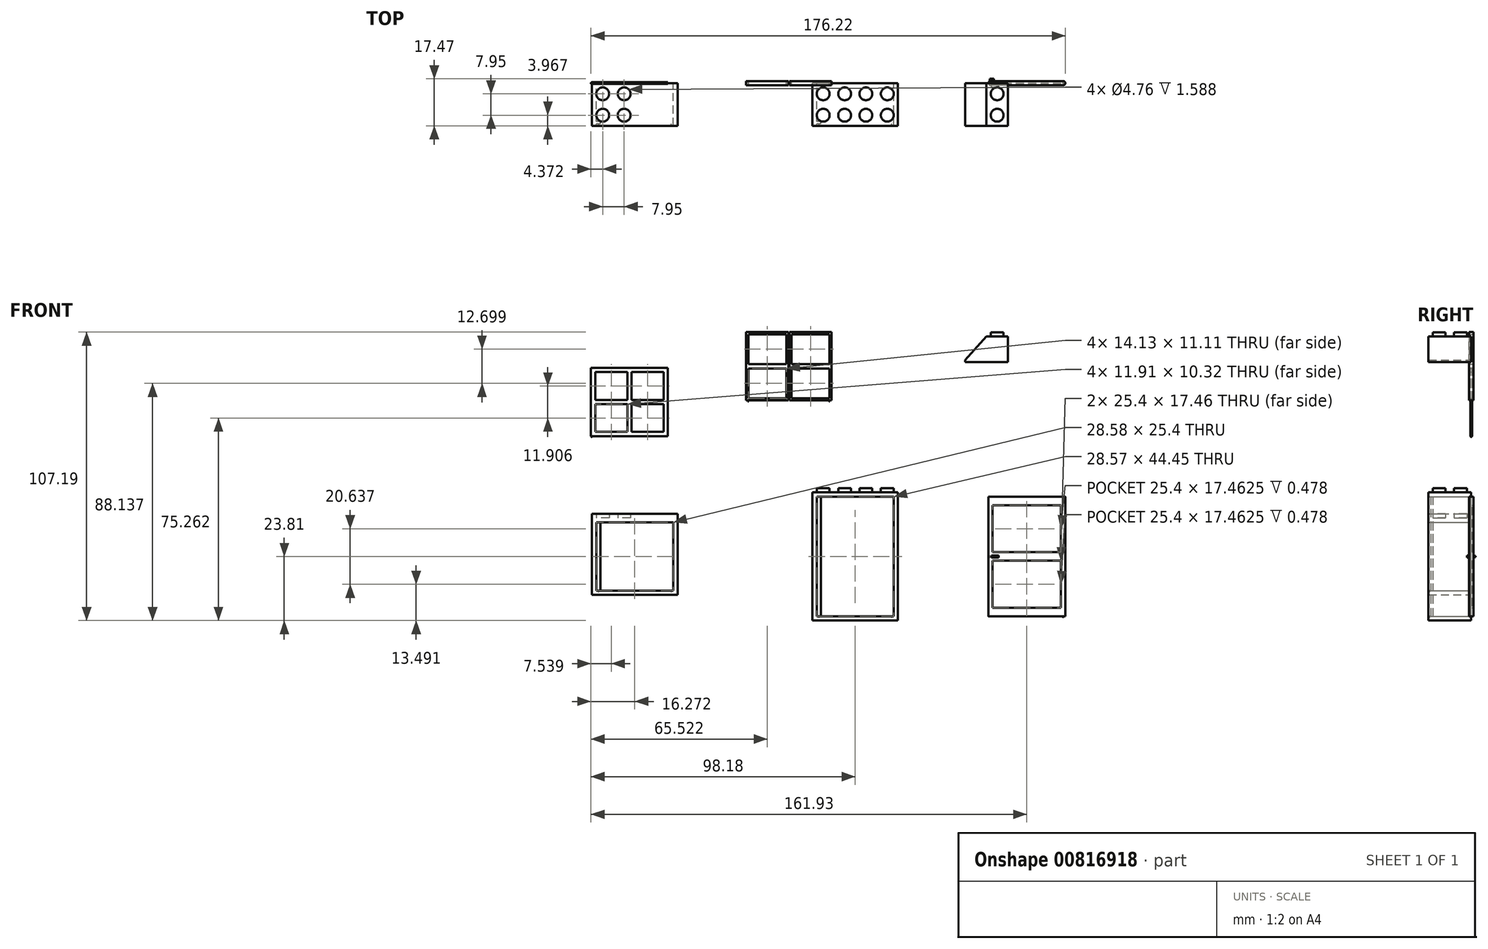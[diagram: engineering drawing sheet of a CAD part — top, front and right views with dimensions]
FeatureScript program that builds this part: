
annotation { "Feature Type Name" : "Feature", "Feature Type Description" : "" }
export const myFeature = defineFeature(function(context is Context, id is Id, definition is map)
    precondition{}
    {
        {
            var Q0;
            Q0=qCreatedBy(makeId("Front.planeOp"),FACE);
            var sketch = newSketch(context, id + "F0", { "sketchPlane" : qUnion([Q0])});
            skLineSegment(sketch, "E0.bottom", {"start": v(15.88, -23.81) * mm, "end": v(-15.87, -23.81) * mm});
            skLineSegment(sketch, "E0.top", {"start": v(15.87, 23.81) * mm, "end": v(-15.88, 23.81) * mm});
            skLineSegment(sketch, "E0.left", {"start": v(15.88, -23.81) * mm, "end": v(15.87, 23.81) * mm});
            skLineSegment(sketch, "E0.right", {"start": v(-15.87, -23.81) * mm, "end": v(-15.88, 23.81) * mm});
            skPoint(sketch, "E0.middle", {"position": v(0, 0) * mm});
            skLineSegment(sketch, "E1.bottom", {"start": v(14.29, -22.22) * mm, "end": v(-14.29, -22.23) * mm});
            skLineSegment(sketch, "E1.top", {"start": v(14.29, 22.23) * mm, "end": v(-14.29, 22.23) * mm});
            skLineSegment(sketch, "E1.left", {"start": v(14.29, -22.22) * mm, "end": v(14.29, 22.23) * mm});
            skLineSegment(sketch, "E1.right", {"start": v(-14.29, -22.23) * mm, "end": v(-14.29, 22.23) * mm});
            skLineSegment(sketch, "E2.bottom", {"start": v(78.04, -22.23) * mm, "end": v(49.46, -22.23) * mm});
            skLineSegment(sketch, "E2.top", {"start": v(78.04, 22.23) * mm, "end": v(49.46, 22.23) * mm});
            skLineSegment(sketch, "E2.left", {"start": v(78.04, -22.23) * mm, "end": v(78.04, 22.23) * mm});
            skLineSegment(sketch, "E2.right", {"start": v(49.46, -22.23) * mm, "end": v(49.46, 22.23) * mm});
            skPoint(sketch, "E2.middle", {"position": v(63.75, 0) * mm});
            skLineSegment(sketch, "E3.bottom", {"start": v(76.45, 1.59) * mm, "end": v(51.05, 1.59) * mm});
            skLineSegment(sketch, "E3.top", {"start": v(76.45, 19.05) * mm, "end": v(51.05, 19.05) * mm});
            skLineSegment(sketch, "E3.left", {"start": v(76.45, 1.59) * mm, "end": v(76.45, 19.05) * mm});
            skLineSegment(sketch, "E3.right", {"start": v(51.05, 1.59) * mm, "end": v(51.05, 19.05) * mm});
            skPoint(sketch, "E3.middle", {"position": v(63.75, 10.32) * mm});
            skPoint(sketch, "E3.middle.positionSnap0", {"position": v(63.75, 22.23) * mm});
            skPoint(sketch, "E3.centerSnap0", {"position": v(63.75, 22.23) * mm});
            skLineSegment(sketch, "E4.bottom", {"start": v(76.45, -1.59) * mm, "end": v(51.05, -1.59) * mm});
            skLineSegment(sketch, "E4.top", {"start": v(76.45, -19.05) * mm, "end": v(51.05, -19.05) * mm});
            skLineSegment(sketch, "E4.left", {"start": v(76.45, -1.59) * mm, "end": v(76.45, -19.05) * mm});
            skLineSegment(sketch, "E4.right", {"start": v(51.05, -1.59) * mm, "end": v(51.05, -19.05) * mm});
            skPoint(sketch, "E4.middle", {"position": v(63.75, -10.32) * mm});
            skPoint(sketch, "E4.middle.positionSnap0", {"position": v(63.75, -22.23) * mm});
            skPoint(sketch, "E4.centerSnap0", {"position": v(63.75, -22.23) * mm});
            skLineSegment(sketch, "E5.bottom", {"start": v(-67.62, -12.7) * mm, "end": v(-96.2, -12.7) * mm});
            skLineSegment(sketch, "E5.top", {"start": v(-67.62, 12.7) * mm, "end": v(-96.2, 12.7) * mm});
            skLineSegment(sketch, "E5.left", {"start": v(-67.62, -12.7) * mm, "end": v(-67.62, 12.7) * mm});
            skLineSegment(sketch, "E5.right", {"start": v(-96.2, -12.7) * mm, "end": v(-96.2, 12.7) * mm});
            skPoint(sketch, "E5.middle", {"position": v(-81.9, 0) * mm});
            skLineSegment(sketch, "E6.bottom", {"start": v(-66.03, -14.29) * mm, "end": v(-97.78, -14.29) * mm});
            skLineSegment(sketch, "E6.top", {"start": v(-66.03, 14.29) * mm, "end": v(-97.78, 14.29) * mm});
            skLineSegment(sketch, "E6.left", {"start": v(-66.03, -14.29) * mm, "end": v(-66.03, 14.29) * mm});
            skLineSegment(sketch, "E6.right", {"start": v(-97.78, -14.29) * mm, "end": v(-97.78, 14.29) * mm});
            skLineSegment(sketch, "E7.bottom", {"start": v(-8.77, 57.98) * mm, "end": v(-24.48, 57.98) * mm});
            skLineSegment(sketch, "E7.top", {"start": v(-8.77, 83.38) * mm, "end": v(-24.48, 83.38) * mm});
            skLineSegment(sketch, "E7.left", {"start": v(-8.77, 57.98) * mm, "end": v(-8.77, 83.38) * mm});
            skLineSegment(sketch, "E7.right", {"start": v(-40.52, 57.98) * mm, "end": v(-40.52, 83.38) * mm});
            skPoint(sketch, "E7.middle", {"position": v(-24.64, 70.68) * mm});
            skLineSegment(sketch, "E8.left", {"start": v(-24.48, 57.98) * mm, "end": v(-24.48, 83.38) * mm});
            skLineSegment(sketch, "E8.right", {"start": v(-24.8, 57.98) * mm, "end": v(-24.8, 83.38) * mm});
            skLineSegment(sketch, "E9.bottom", {"start": v(-9.56, 69.88) * mm, "end": v(-23.69, 69.88) * mm});
            skLineSegment(sketch, "E9.top", {"start": v(-9.56, 71.47) * mm, "end": v(-23.69, 71.47) * mm});
            skLineSegment(sketch, "E9.left", {"start": v(-8.77, 69.88) * mm, "end": v(-8.77, 71.47) * mm});
            skLineSegment(sketch, "E9.right", {"start": v(-40.52, 69.88) * mm, "end": v(-40.52, 71.47) * mm});
            skLineSegment(sketch, "E10", {"start": v(-39.72, 58.77) * mm, "end": v(-25.6, 58.77) * mm});
            skLineSegment(sketch, "E11", {"start": v(-9.56, 82.58) * mm, "end": v(-23.69, 82.58) * mm});
            skLineSegment(sketch, "E12", {"start": v(-9.56, 82.58) * mm, "end": v(-9.56, 71.47) * mm});
            skLineSegment(sketch, "E13", {"start": v(-39.72, 82.58) * mm, "end": v(-39.72, 71.47) * mm});
            skLineSegment(sketch, "E14", {"start": v(-23.69, 82.58) * mm, "end": v(-23.69, 71.47) * mm});
            skLineSegment(sketch, "E15", {"start": v(-25.6, 82.58) * mm, "end": v(-25.6, 71.47) * mm});
            skLineSegment(sketch, "E16.trimOffspring", {"start": v(-25.6, 82.58) * mm, "end": v(-39.72, 82.58) * mm});
            skPoint(sketch, "E17.orphan", {"position": v(-8.77, 82.58) * mm});
            skPoint(sketch, "E18.orphan", {"position": v(-8.77, 58.77) * mm});
            skLineSegment(sketch, "E19.trimOffspring", {"start": v(-23.69, 58.77) * mm, "end": v(-9.56, 58.77) * mm});
            skLineSegment(sketch, "E20.trimOffspring", {"start": v(-24.8, 57.98) * mm, "end": v(-40.52, 57.98) * mm});
            skLineSegment(sketch, "E21.trimOffspring", {"start": v(-25.6, 69.88) * mm, "end": v(-39.72, 69.88) * mm});
            skLineSegment(sketch, "E22.trimOffspring", {"start": v(-25.6, 71.47) * mm, "end": v(-39.72, 71.47) * mm});
            skLineSegment(sketch, "E23.trimOffspring", {"start": v(-24.8, 83.38) * mm, "end": v(-40.52, 83.38) * mm});
            skPoint(sketch, "E24.orphan", {"position": v(-40.52, 82.58) * mm});
            skLineSegment(sketch, "E25.trimOffspring", {"start": v(-39.72, 69.88) * mm, "end": v(-39.72, 58.77) * mm});
            skLineSegment(sketch, "E26.trimOffspring", {"start": v(-25.6, 69.88) * mm, "end": v(-25.6, 58.77) * mm});
            skLineSegment(sketch, "E27.trimOffspring", {"start": v(-23.69, 69.88) * mm, "end": v(-23.69, 58.77) * mm});
            skLineSegment(sketch, "E28.trimOffspring", {"start": v(-9.56, 69.88) * mm, "end": v(-9.56, 58.77) * mm});
            skLineSegment(sketch, "E29.bottom", {"start": v(56.7, 72.23) * mm, "end": v(40.82, 72.23) * mm});
            skLineSegment(sketch, "E29.top", {"start": v(56.7, 81.75) * mm, "end": v(48.76, 81.75) * mm});
            skLineSegment(sketch, "E29.left", {"start": v(56.7, 72.23) * mm, "end": v(56.7, 81.75) * mm});
            skLineSegment(sketch, "E29.right", {"start": v(40.82, 72.23) * mm, "end": v(40.82, 73.02) * mm});
            skPoint(sketch, "E29.middle", {"position": v(48.76, 77) * mm});
            skLineSegment(sketch, "E30", {"start": v(40.82, 73.02) * mm, "end": v(48.76, 81.75) * mm});
            skPoint(sketch, "E31.orphan", {"position": v(40.82, 81.75) * mm});
            skLineSegment(sketch, "E32.bottom", {"start": v(-69.6, 44.7) * mm, "end": v(-98.18, 44.7) * mm});
            skLineSegment(sketch, "E32.top", {"start": v(-69.6, 70.1) * mm, "end": v(-98.18, 70.1) * mm});
            skLineSegment(sketch, "E32.left", {"start": v(-69.6, 44.7) * mm, "end": v(-69.6, 70.1) * mm});
            skLineSegment(sketch, "E32.right", {"start": v(-98.18, 44.7) * mm, "end": v(-98.18, 70.1) * mm});
            skPoint(sketch, "E32.middle", {"position": v(-83.9, 57.4) * mm});
            skLineSegment(sketch, "E33.bottom", {"start": v(-71.2, 46.3) * mm, "end": v(-83.1, 46.3) * mm});
            skLineSegment(sketch, "E33.top", {"start": v(-71.2, 68.52) * mm, "end": v(-83.1, 68.52) * mm});
            skLineSegment(sketch, "E33.left", {"start": v(-71.2, 46.3) * mm, "end": v(-71.2, 56.61) * mm});
            skLineSegment(sketch, "E33.right", {"start": v(-96.6, 46.3) * mm, "end": v(-96.6, 56.61) * mm});
            skLineSegment(sketch, "E34.bottom", {"start": v(-71.2, 58.2) * mm, "end": v(-83.1, 58.2) * mm});
            skLineSegment(sketch, "E34.top", {"start": v(-71.2, 56.61) * mm, "end": v(-83.1, 56.61) * mm});
            skLineSegment(sketch, "E35.left", {"start": v(-83.1, 46.3) * mm, "end": v(-83.1, 56.61) * mm});
            skLineSegment(sketch, "E35.right", {"start": v(-84.69, 46.3) * mm, "end": v(-84.69, 56.61) * mm});
            skLineSegment(sketch, "E36.trimOffspring", {"start": v(-83.1, 58.2) * mm, "end": v(-83.1, 68.52) * mm});
            skLineSegment(sketch, "E37.trimOffspring", {"start": v(-84.69, 58.2) * mm, "end": v(-84.69, 68.52) * mm});
            skLineSegment(sketch, "E38.trimOffspring", {"start": v(-84.69, 58.2) * mm, "end": v(-96.6, 58.2) * mm});
            skLineSegment(sketch, "E39.trimOffspring", {"start": v(-84.69, 56.61) * mm, "end": v(-96.6, 56.61) * mm});
            skLineSegment(sketch, "E40.trimOffspring", {"start": v(-71.2, 58.2) * mm, "end": v(-71.2, 68.52) * mm});
            skLineSegment(sketch, "E41.trimOffspring", {"start": v(-96.6, 58.2) * mm, "end": v(-96.6, 68.52) * mm});
            skLineSegment(sketch, "E42.trimOffspring", {"start": v(-84.69, 46.3) * mm, "end": v(-96.6, 46.3) * mm});
            skLineSegment(sketch, "E43.trimOffspring", {"start": v(-84.69, 68.52) * mm, "end": v(-96.6, 68.52) * mm});
            skSolve(sketch);
        }
        {
            var Q0;
            Q0=makeQuery(id+"F0.imprint","IMPRINT",FACE,{"disambiguationData":[TD([[makeQuery(id+"F0.imprint","IMPRINT",EDGE,{"derivedFrom":sQuery(id+"F0.wireOp",EDGE,"E0.bottom")}),-1.0]])]});
            extrude(context, id + "F1", {"entities" : qUnion([Q0]), "depth" : 15.88 * mm, "offsetDistance" : 25.4 * mm});
        }
        {
            var Q0;
            Q0=makeQuery(id+"F0.imprint","IMPRINT",FACE,{"disambiguationData":[TD([[makeQuery(id+"F0.imprint","IMPRINT",EDGE,{"derivedFrom":sQuery(id+"F0.wireOp",EDGE,"E5.bottom")}),1.0]])]});
            extrude(context, id + "F2", {"entities" : qUnion([Q0]), "depth" : 15.88 * mm, "offsetDistance" : 25.4 * mm});
        }
        {
            var Q0;
            Q0=makeQuery(id+"F1.opExtrude","SWEPT_FACE",FACE,{"disambiguationData":[OSD([sQuery(id+"F0.wireOp",EDGE,"E0.top")])]});
            var sketch = newSketch(context, id + "F3", { "sketchPlane" : qUnion([Q0])});
            skLineSegment(sketch, "E44.bottom", {"start": v(-15.88, -15.88) * mm, "end": v(15.88, -15.88) * mm, "construction": true});
            skLineSegment(sketch, "E44.top", {"start": v(-15.88, 0) * mm, "end": v(15.88, 0) * mm, "construction": true});
            skLineSegment(sketch, "E44.left", {"start": v(-15.88, -15.88) * mm, "end": v(-15.88, 0) * mm, "construction": true});
            skLineSegment(sketch, "E44.right", {"start": v(15.87, -15.88) * mm, "end": v(15.87, 0) * mm, "construction": true});
            skLineSegment(sketch, "E45", {"start": v(0, -15.88) * mm, "end": v(0, 0) * mm, "construction": true});
            skLineSegment(sketch, "E46", {"start": v(-15.88, -7.94) * mm, "end": v(15.88, -7.94) * mm, "construction": true});
            skLineSegment(sketch, "E47.bottom", {"start": v(-3.96, -11.91) * mm, "end": v(-11.9, -11.91) * mm});
            skLineSegment(sketch, "E47.top", {"start": v(-3.96, -3.96) * mm, "end": v(-11.9, -3.96) * mm});
            skLineSegment(sketch, "E47.left", {"start": v(-3.96, -11.91) * mm, "end": v(-3.96, -3.96) * mm});
            skLineSegment(sketch, "E47.right", {"start": v(-11.9, -11.91) * mm, "end": v(-11.9, -3.96) * mm});
            skPoint(sketch, "E47.middle", {"position": v(-7.93, -7.94) * mm});
            skLineSegment(sketch, "E48.bottom", {"start": v(11.9, -11.91) * mm, "end": v(3.95, -11.91) * mm});
            skLineSegment(sketch, "E48.top", {"start": v(11.9, -3.96) * mm, "end": v(3.95, -3.96) * mm});
            skLineSegment(sketch, "E48.left", {"start": v(11.9, -11.91) * mm, "end": v(11.9, -3.96) * mm});
            skLineSegment(sketch, "E48.right", {"start": v(3.95, -11.91) * mm, "end": v(3.95, -3.96) * mm});
            skPoint(sketch, "E48.middle", {"position": v(7.92, -7.94) * mm});
            skCircle(sketch, "E49", {"center": v(-11.9, -3.96) * mm, "radius": 2.38 * mm});
            skCircle(sketch, "E50", {"center": v(-11.9, -11.91) * mm, "radius": 2.38 * mm});
            skCircle(sketch, "E51", {"center": v(-3.96, -11.91) * mm, "radius": 2.38 * mm});
            skCircle(sketch, "E52", {"center": v(-3.96, -3.96) * mm, "radius": 2.38 * mm});
            skCircle(sketch, "E53", {"center": v(3.95, -11.91) * mm, "radius": 2.38 * mm});
            skCircle(sketch, "E54", {"center": v(11.9, -11.91) * mm, "radius": 2.38 * mm});
            skCircle(sketch, "E55", {"center": v(11.9, -3.96) * mm, "radius": 2.38 * mm});
            skCircle(sketch, "E56", {"center": v(3.95, -3.96) * mm, "radius": 2.38 * mm});
            skPoint(sketch, "E57.middle", {"position": v(-89.84, -7.94) * mm});
            skPoint(sketch, "E58.middle", {"position": v(-73.98, -7.94) * mm});
            skPoint(sketch, "E59.left.end.orphan", {"position": v(-97.78, -7.94) * mm});
            skPoint(sketch, "E59.left.start.orphan", {"position": v(-97.78, -15.88) * mm});
            skPoint(sketch, "E57.bottom.end.orphan", {"position": v(-93.81, -11.91) * mm});
            skPoint(sketch, "E57.bottom.start.orphan", {"position": v(-85.86, -11.91) * mm});
            skPoint(sketch, "E57.top.end.orphan", {"position": v(-93.81, -3.96) * mm});
            skPoint(sketch, "E57.top.start.orphan", {"position": v(-85.86, -3.96) * mm});
            skPoint(sketch, "E60.orphan", {"position": v(-77.96, -3.96) * mm});
            skPoint(sketch, "E61.center.orphan", {"position": v(-70, -3.96) * mm});
            skPoint(sketch, "E62.trimOffspring.end.orphan", {"position": v(-66.03, -7.94) * mm});
            skPoint(sketch, "E63.orphan", {"position": v(-70, -11.91) * mm});
            skPoint(sketch, "E64.center.orphan", {"position": v(-77.96, -11.91) * mm});
            skPoint(sketch, "E59.bottom.start.orphan", {"position": v(-81.9, -15.88) * mm});
            skPoint(sketch, "E65.orphan", {"position": v(-66.03, -15.88) * mm});
            skPoint(sketch, "E59.right.end.orphan", {"position": v(-66.03, 0) * mm});
            skSolve(sketch);
        }
        {
            var Q0;
            {var subQ0=sQuery(id+"F3.wireOp",EDGE,"E47.right");var subQ1=sQuery(id+"F3.wireOp",EDGE,"E47.top");var subQ2=makeQuery(id+"F3.imprint","INTERSECT",VERTEX,{"derivedFrom":[subQ1,subQ0]});Q0=makeQuery(id+"F3.imprint","IMPRINT",FACE,{"disambiguationData":[TD([[makeQuery(id+"F3.imprint","IMPRINT",EDGE,{"disambiguationData":[TD([[subQ2,1.0]])],"derivedFrom":subQ1}),-1.0]])]});}
            var Q1;
            {var subQ0=sQuery(id+"F3.wireOp",EDGE,"E47.right");var subQ1=sQuery(id+"F3.wireOp",EDGE,"E47.bottom");var subQ2=makeQuery(id+"F3.imprint","INTERSECT",VERTEX,{"derivedFrom":[subQ1,subQ0]});Q1=makeQuery(id+"F3.imprint","IMPRINT",FACE,{"disambiguationData":[TD([[makeQuery(id+"F3.imprint","IMPRINT",EDGE,{"disambiguationData":[TD([[subQ2,1.0]])],"derivedFrom":subQ1}),1.0]])]});}
            var Q2;
            {var subQ0=sQuery(id+"F3.wireOp",EDGE,"E47.right");var subQ1=sQuery(id+"F3.wireOp",EDGE,"E47.top");var subQ2=makeQuery(id+"F3.imprint","INTERSECT",VERTEX,{"derivedFrom":[subQ1,subQ0]});Q2=makeQuery(id+"F3.imprint","IMPRINT",FACE,{"disambiguationData":[TD([[makeQuery(id+"F3.imprint","IMPRINT",EDGE,{"disambiguationData":[TD([[subQ2,1.0]])],"derivedFrom":subQ1}),1.0]])]});}
            var Q3;
            {var subQ0=sQuery(id+"F3.wireOp",EDGE,"E47.left");var subQ1=sQuery(id+"F3.wireOp",EDGE,"E47.top");var subQ2=makeQuery(id+"F3.imprint","INTERSECT",VERTEX,{"derivedFrom":[subQ1,subQ0]});Q3=makeQuery(id+"F3.imprint","IMPRINT",FACE,{"disambiguationData":[TD([[makeQuery(id+"F3.imprint","IMPRINT",EDGE,{"disambiguationData":[TD([[subQ2,-1.0]])],"derivedFrom":subQ1}),-1.0]])]});}
            var Q4;
            {var subQ0=sQuery(id+"F3.wireOp",EDGE,"E47.left");var subQ1=sQuery(id+"F3.wireOp",EDGE,"E47.bottom");var subQ2=makeQuery(id+"F3.imprint","INTERSECT",VERTEX,{"derivedFrom":[subQ1,subQ0]});Q4=makeQuery(id+"F3.imprint","IMPRINT",FACE,{"disambiguationData":[TD([[makeQuery(id+"F3.imprint","IMPRINT",EDGE,{"disambiguationData":[TD([[subQ2,-1.0]])],"derivedFrom":subQ1}),1.0]])]});}
            var Q5;
            {var subQ0=sQuery(id+"F3.wireOp",EDGE,"E48.right");var subQ1=sQuery(id+"F3.wireOp",EDGE,"E48.bottom");var subQ2=makeQuery(id+"F3.imprint","INTERSECT",VERTEX,{"derivedFrom":[subQ1,subQ0]});Q5=makeQuery(id+"F3.imprint","IMPRINT",FACE,{"disambiguationData":[TD([[makeQuery(id+"F3.imprint","IMPRINT",EDGE,{"disambiguationData":[TD([[subQ2,1.0]])],"derivedFrom":subQ1}),1.0]])]});}
            var Q6;
            {var subQ0=sQuery(id+"F3.wireOp",EDGE,"E48.left");var subQ1=sQuery(id+"F3.wireOp",EDGE,"E48.bottom");var subQ2=makeQuery(id+"F3.imprint","INTERSECT",VERTEX,{"derivedFrom":[subQ1,subQ0]});Q6=makeQuery(id+"F3.imprint","IMPRINT",FACE,{"disambiguationData":[TD([[makeQuery(id+"F3.imprint","IMPRINT",EDGE,{"disambiguationData":[TD([[subQ2,-1.0]])],"derivedFrom":subQ1}),-1.0]])]});}
            var Q7;
            {var subQ0=sQuery(id+"F3.wireOp",EDGE,"E48.left");var subQ1=sQuery(id+"F3.wireOp",EDGE,"E48.bottom");var subQ2=makeQuery(id+"F3.imprint","INTERSECT",VERTEX,{"derivedFrom":[subQ1,subQ0]});Q7=makeQuery(id+"F3.imprint","IMPRINT",FACE,{"disambiguationData":[TD([[makeQuery(id+"F3.imprint","IMPRINT",EDGE,{"disambiguationData":[TD([[subQ2,-1.0]])],"derivedFrom":subQ1}),1.0]])]});}
            var Q8;
            {var subQ0=sQuery(id+"F3.wireOp",EDGE,"E48.right");var subQ1=sQuery(id+"F3.wireOp",EDGE,"E48.bottom");var subQ2=makeQuery(id+"F3.imprint","INTERSECT",VERTEX,{"derivedFrom":[subQ1,subQ0]});Q8=makeQuery(id+"F3.imprint","IMPRINT",FACE,{"disambiguationData":[TD([[makeQuery(id+"F3.imprint","IMPRINT",EDGE,{"disambiguationData":[TD([[subQ2,1.0]])],"derivedFrom":subQ1}),-1.0]])]});}
            var Q9;
            {var subQ0=sQuery(id+"F3.wireOp",EDGE,"E48.right");var subQ1=sQuery(id+"F3.wireOp",EDGE,"E48.top");var subQ2=makeQuery(id+"F3.imprint","INTERSECT",VERTEX,{"derivedFrom":[subQ1,subQ0]});Q9=makeQuery(id+"F3.imprint","IMPRINT",FACE,{"disambiguationData":[TD([[makeQuery(id+"F3.imprint","IMPRINT",EDGE,{"disambiguationData":[TD([[subQ2,1.0]])],"derivedFrom":subQ1}),-1.0]])]});}
            var Q10;
            {var subQ0=sQuery(id+"F3.wireOp",EDGE,"E48.left");var subQ1=sQuery(id+"F3.wireOp",EDGE,"E48.top");var subQ2=makeQuery(id+"F3.imprint","INTERSECT",VERTEX,{"derivedFrom":[subQ1,subQ0]});Q10=makeQuery(id+"F3.imprint","IMPRINT",FACE,{"disambiguationData":[TD([[makeQuery(id+"F3.imprint","IMPRINT",EDGE,{"disambiguationData":[TD([[subQ2,-1.0]])],"derivedFrom":subQ1}),1.0]])]});}
            var Q11;
            {var subQ0=sQuery(id+"F3.wireOp",EDGE,"E47.right");var subQ1=sQuery(id+"F3.wireOp",EDGE,"E47.bottom");var subQ2=makeQuery(id+"F3.imprint","INTERSECT",VERTEX,{"derivedFrom":[subQ1,subQ0]});Q11=makeQuery(id+"F3.imprint","IMPRINT",FACE,{"disambiguationData":[TD([[makeQuery(id+"F3.imprint","IMPRINT",EDGE,{"disambiguationData":[TD([[subQ2,1.0]])],"derivedFrom":subQ1}),-1.0]])]});}
            var Q12;
            {var subQ0=sQuery(id+"F3.wireOp",EDGE,"E47.left");var subQ1=sQuery(id+"F3.wireOp",EDGE,"E47.bottom");var subQ2=makeQuery(id+"F3.imprint","INTERSECT",VERTEX,{"derivedFrom":[subQ1,subQ0]});Q12=makeQuery(id+"F3.imprint","IMPRINT",FACE,{"disambiguationData":[TD([[makeQuery(id+"F3.imprint","IMPRINT",EDGE,{"disambiguationData":[TD([[subQ2,-1.0]])],"derivedFrom":subQ1}),-1.0]])]});}
            var Q13;
            {var subQ0=sQuery(id+"F3.wireOp",EDGE,"E47.left");var subQ1=sQuery(id+"F3.wireOp",EDGE,"E47.top");var subQ2=makeQuery(id+"F3.imprint","INTERSECT",VERTEX,{"derivedFrom":[subQ1,subQ0]});Q13=makeQuery(id+"F3.imprint","IMPRINT",FACE,{"disambiguationData":[TD([[makeQuery(id+"F3.imprint","IMPRINT",EDGE,{"disambiguationData":[TD([[subQ2,-1.0]])],"derivedFrom":subQ1}),1.0]])]});}
            var Q14;
            {var subQ0=sQuery(id+"F3.wireOp",EDGE,"E48.left");var subQ1=sQuery(id+"F3.wireOp",EDGE,"E48.top");var subQ2=makeQuery(id+"F3.imprint","INTERSECT",VERTEX,{"derivedFrom":[subQ1,subQ0]});Q14=makeQuery(id+"F3.imprint","IMPRINT",FACE,{"disambiguationData":[TD([[makeQuery(id+"F3.imprint","IMPRINT",EDGE,{"disambiguationData":[TD([[subQ2,-1.0]])],"derivedFrom":subQ1}),-1.0]])]});}
            var Q15;
            {var subQ0=sQuery(id+"F3.wireOp",EDGE,"E48.right");var subQ1=sQuery(id+"F3.wireOp",EDGE,"E48.top");var subQ2=makeQuery(id+"F3.imprint","INTERSECT",VERTEX,{"derivedFrom":[subQ1,subQ0]});Q15=makeQuery(id+"F3.imprint","IMPRINT",FACE,{"disambiguationData":[TD([[makeQuery(id+"F3.imprint","IMPRINT",EDGE,{"disambiguationData":[TD([[subQ2,1.0]])],"derivedFrom":subQ1}),1.0]])]});}
            extrude(context, id + "F4", {"entities" : qUnion([Q0, Q1, Q2, Q3, Q4, Q5, Q6, Q7, Q8, Q9, Q10, Q11, Q12, Q13, Q14, Q15]), "operationType" : NewBodyOperationType.ADD, "depth" : 1.59 * mm, "offsetDistance" : 25.4 * mm});
        }
        {
            var Q0;
            Q0=makeQuery(id+"F1.opExtrude","SWEPT_FACE",FACE,{"disambiguationData":[OSD([sQuery(id+"F0.wireOp",EDGE,"E1.bottom")])]});
            var sketch = newSketch(context, id + "F5", { "sketchPlane" : qUnion([Q0])});
            skLineSegment(sketch, "E66.top", {"start": v(14.29, -14.28) * mm, "end": v(12.7, -14.28) * mm});
            skLineSegment(sketch, "E66.left", {"start": v(14.29, -15.08) * mm, "end": v(14.29, -14.28) * mm});
            skLineSegment(sketch, "E66.right", {"start": v(12.7, -15.08) * mm, "end": v(12.7, -14.28) * mm});
            skLineSegment(sketch, "E67.bottom", {"start": v(12.7, -14.28) * mm, "end": v(14.29, -14.28) * mm});
            skLineSegment(sketch, "E67.top", {"start": v(12.7, -15.08) * mm, "end": v(14.29, -15.08) * mm});
            skLineSegment(sketch, "E67.left", {"start": v(12.7, -14.28) * mm, "end": v(12.7, -15.08) * mm});
            skLineSegment(sketch, "E67.right", {"start": v(14.29, -14.28) * mm, "end": v(14.29, -15.08) * mm});
            skPoint(sketch, "E68", {"position": v(13.5, -15.48) * mm});
            skPoint(sketch, "E69.orphan", {"position": v(14.29, -15.88) * mm});
            skPoint(sketch, "E70.MirrorP", {"position": v(-13.5, -15.48) * mm});
            skLineSegment(sketch, "E71.MirrorCS", {"start": v(-12.7, -15.08) * mm, "end": v(-14.29, -15.08) * mm});
            skLineSegment(sketch, "E72.MirrorCS", {"start": v(-12.7, -15.08) * mm, "end": v(-12.7, -14.28) * mm});
            skLineSegment(sketch, "E73.MirrorCS", {"start": v(-12.7, -14.28) * mm, "end": v(-14.29, -14.28) * mm});
            skLineSegment(sketch, "E74.MirrorCS", {"start": v(-14.29, -14.28) * mm, "end": v(-14.29, -15.08) * mm});
            skSolve(sketch);
        }
        {
            var Q0;
            Q0=makeQuery(id+"F5.imprint","IMPRINT",FACE,{"disambiguationData":[TD([[makeQuery(id+"F5.imprint","IMPRINT",EDGE,{"derivedFrom":sQuery(id+"F5.wireOp",EDGE,"E67.bottom")}),-1.0]])]});
            var Q1;
            Q1=makeQuery(id+"F5.imprint","IMPRINT",FACE,{"disambiguationData":[TD([[makeQuery(id+"F5.imprint","IMPRINT",EDGE,{"derivedFrom":sQuery(id+"F5.wireOp",EDGE,"E71.MirrorCS")}),-1.0]])]});
            extrude(context, id + "F6", {"entities" : qUnion([Q0, Q1]), "operationType" : NewBodyOperationType.ADD, "depth" : 44.45 * mm, "offsetDistance" : 25.4 * mm});
        }
        {
            var Q0;
            Q0=sQuery(id+"F5.wireOp",VERTEX,"E70.MirrorP");
            var Q1;
            Q1=sQuery(id+"F5.wireOp",VERTEX,"E68");
            var Q2;
            Q2=makeQuery(id+"F1.opExtrude","SWEPT_BODY",BODY,{"disambiguationData":[OSD([sQuery(id+"F0.wireOp",EDGE,"E0.bottom"),sQuery(id+"F0.wireOp",EDGE,"E0.top"),sQuery(id+"F0.wireOp",EDGE,"E0.left"),sQuery(id+"F0.wireOp",EDGE,"E0.right"),sQuery(id+"F0.wireOp",EDGE,"E1.bottom"),sQuery(id+"F0.wireOp",EDGE,"E1.top"),sQuery(id+"F0.wireOp",EDGE,"E1.left"),sQuery(id+"F0.wireOp",EDGE,"E1.right")])]});
            hole(context, id + "F7", {"style" : HoleStyle.SIMPLE, "endStyle" : HoleEndStyle.BLIND, "standardTappedOrClearance" : lookupTablePath({ "standard" : "Custom", "fit" : "Normal", "size" : "M5", "type" : "Clearance" }), "standardBlindInLast" : lookupTablePath({ "fit" : "Standard", "standard" : "Custom", "size" : "M5", "type" : "Clearance" }), "holeDiameter" : 0.32 * mm, "majorDiameter" : 6.35 * mm, "holeDepth" : 0.32 * mm, "isTappedThrough" : true, "tappedDepth" : 12.7 * mm, "tapClearance" : 3, "locations" : qUnion([Q0, Q1]), "scope" : qUnion([Q2])});
        }
        {
            var Q0;
            Q0=makeQuery(id+"F0.imprint","IMPRINT",FACE,{"disambiguationData":[TD([[makeQuery(id+"F0.imprint","IMPRINT",EDGE,{"derivedFrom":sQuery(id+"F0.wireOp",EDGE,"E2.bottom")}),-1.0]])]});
            extrude(context, id + "F8", {"entities" : qUnion([Q0]), "depth" : 0.8 * mm, "offsetDistance" : 25.4 * mm});
        }
        {
            var Q0;
            Q0=makeQuery(id+"F0.imprint","IMPRINT",FACE,{"disambiguationData":[TD([[makeQuery(id+"F0.imprint","IMPRINT",EDGE,{"derivedFrom":sQuery(id+"F0.wireOp",EDGE,"E2.bottom")}),-1.0]])]});
            extrude(context, id + "F9", {"entities" : qUnion([Q0]), "operationType" : NewBodyOperationType.ADD, "oppositeDirection" : true, "depth" : 0.8 * mm, "offsetDistance" : 25.4 * mm});
        }
        {
            var Q0;
            Q0=makeQuery(id+"F0.imprint","IMPRINT",FACE,{"disambiguationData":[TD([[makeQuery(id+"F0.imprint","IMPRINT",EDGE,{"derivedFrom":sQuery(id+"F0.wireOp",EDGE,"E3.bottom")}),-1.0]])]});
            var Q1;
            Q1=makeQuery(id+"F0.imprint","IMPRINT",FACE,{"disambiguationData":[TD([[makeQuery(id+"F0.imprint","IMPRINT",EDGE,{"derivedFrom":sQuery(id+"F0.wireOp",EDGE,"E4.bottom")}),1.0]])]});
            extrude(context, id + "F10", {"entities" : qUnion([Q0, Q1]), "operationType" : NewBodyOperationType.ADD, "depth" : 0.32 * mm, "offsetDistance" : 25.4 * mm});
        }
        {
            var Q0;
            Q0=makeQuery(id+"F0.imprint","IMPRINT",FACE,{"disambiguationData":[TD([[makeQuery(id+"F0.imprint","IMPRINT",EDGE,{"derivedFrom":sQuery(id+"F0.wireOp",EDGE,"E4.bottom")}),1.0]])]});
            var Q1;
            Q1=makeQuery(id+"F0.imprint","IMPRINT",FACE,{"disambiguationData":[TD([[makeQuery(id+"F0.imprint","IMPRINT",EDGE,{"derivedFrom":sQuery(id+"F0.wireOp",EDGE,"E3.bottom")}),-1.0]])]});
            extrude(context, id + "F11", {"entities" : qUnion([Q0, Q1]), "operationType" : NewBodyOperationType.ADD, "oppositeDirection" : true, "depth" : 0.32 * mm, "offsetDistance" : 25.4 * mm});
        }
        {
            var Q0;
            Q0=makeQuery(id+"F8.opExtrude","CAP_FACE",FACE,{"disambiguationData":[OSD([sQuery(id+"F0.wireOp",EDGE,"E2.bottom"),sQuery(id+"F0.wireOp",EDGE,"E2.top"),sQuery(id+"F0.wireOp",EDGE,"E2.left"),sQuery(id+"F0.wireOp",EDGE,"E2.right"),sQuery(id+"F0.wireOp",EDGE,"E3.bottom"),sQuery(id+"F0.wireOp",EDGE,"E3.top"),sQuery(id+"F0.wireOp",EDGE,"E3.left"),sQuery(id+"F0.wireOp",EDGE,"E3.right"),sQuery(id+"F0.wireOp",EDGE,"E4.bottom"),sQuery(id+"F0.wireOp",EDGE,"E4.top"),sQuery(id+"F0.wireOp",EDGE,"E4.left"),sQuery(id+"F0.wireOp",EDGE,"E4.right")])],"isStart":false});
            var sketch = newSketch(context, id + "F12", { "sketchPlane" : qUnion([Q0])});
            skLineSegment(sketch, "E75.bottom", {"start": v(53.26, -0.4) * mm, "end": v(50.66, -0.4) * mm});
            skLineSegment(sketch, "E75.top", {"start": v(53.26, 0.4) * mm, "end": v(50.66, 0.4) * mm});
            skLineSegment(sketch, "E75.left", {"start": v(53.26, -0.4) * mm, "end": v(53.26, 0.4) * mm});
            skLineSegment(sketch, "E75.right", {"start": v(50.66, -0.4) * mm, "end": v(50.66, 0.4) * mm});
            skPoint(sketch, "E75.middle", {"position": v(51.96, 0) * mm});
            skSolve(sketch);
        }
        {
            var Q0;
            Q0=makeQuery(id+"F12.imprint","IMPRINT",FACE,{"disambiguationData":[TD([[makeQuery(id+"F12.imprint","IMPRINT",EDGE,{"derivedFrom":sQuery(id+"F12.wireOp",EDGE,"E75.bottom")}),-1.0]])]});
            extrude(context, id + "F13", {"entities" : qUnion([Q0]), "operationType" : NewBodyOperationType.ADD, "depth" : 0.8 * mm, "offsetDistance" : 25.4 * mm});
        }
        {
            var Q0;
            Q0=makeQuery(id+"F9.opExtrude","CAP_FACE",FACE,{"disambiguationData":[OSD([sQuery(id+"F0.wireOp",EDGE,"E2.bottom"),sQuery(id+"F0.wireOp",EDGE,"E2.top"),sQuery(id+"F0.wireOp",EDGE,"E2.left"),sQuery(id+"F0.wireOp",EDGE,"E2.right"),sQuery(id+"F0.wireOp",EDGE,"E3.bottom"),sQuery(id+"F0.wireOp",EDGE,"E3.top"),sQuery(id+"F0.wireOp",EDGE,"E3.left"),sQuery(id+"F0.wireOp",EDGE,"E3.right"),sQuery(id+"F0.wireOp",EDGE,"E4.bottom"),sQuery(id+"F0.wireOp",EDGE,"E4.top"),sQuery(id+"F0.wireOp",EDGE,"E4.left"),sQuery(id+"F0.wireOp",EDGE,"E4.right")])],"isStart":false});
            var sketch = newSketch(context, id + "F14", { "sketchPlane" : qUnion([Q0])});
            skLineSegment(sketch, "E76.bottom", {"start": v(-49.93, -0.3) * mm, "end": v(-51.5, -0.3) * mm});
            skLineSegment(sketch, "E76.top", {"start": v(-49.93, 0.3) * mm, "end": v(-51.5, 0.3) * mm});
            skLineSegment(sketch, "E76.left", {"start": v(-49.93, -0.3) * mm, "end": v(-49.93, 0.3) * mm});
            skLineSegment(sketch, "E76.right", {"start": v(-51.5, -0.3) * mm, "end": v(-51.5, 0.3) * mm});
            skPoint(sketch, "E76.middle", {"position": v(-50.72, 0) * mm});
            skSolve(sketch);
        }
        {
            var Q0;
            Q0=makeQuery(id+"F14.imprint","IMPRINT",FACE,{"disambiguationData":[TD([[makeQuery(id+"F14.imprint","IMPRINT",EDGE,{"derivedFrom":sQuery(id+"F14.wireOp",EDGE,"E76.bottom")}),-1.0]])]});
            var Q1;
            Q1 = qSketchRegion(id + "F14", true);
            extrude(context, id + "F15", {"entities" : qUnion([Q0, Q1]), "operationType" : NewBodyOperationType.ADD, "depth" : 0.8 * mm, "offsetDistance" : 25.4 * mm});
        }
        {
            var Q0;
            Q0=makeQuery(id+"F8.opExtrude","CAP_EDGE",EDGE,{"disambiguationData":[OSD([sQuery(id+"F0.wireOp",EDGE,"E2.left")])],"isStart":false});
            var Q1;
            Q1=makeQuery(id+"F9.opExtrude","CAP_EDGE",EDGE,{"disambiguationData":[OSD([sQuery(id+"F0.wireOp",EDGE,"E2.left")])],"isStart":false});
            fillet(context, id + "F16", {"entities" : qUnion([Q0, Q1]), "radius" : 0.8 * mm, "tangentPropagation" : true, "allowEdgeOverflow" : false});
        }
        {
            var Q0;
            {var subQ0=sQuery(id+"F0.wireOp",EDGE,"E2.bottom");Q0=makeQuery(id+"F9.boolean.opBoolean","MERGE",FACE,{"derivedFrom":[makeQuery(id+"F8.opExtrude","SWEPT_FACE",FACE,{"disambiguationData":[OSD([subQ0])]}),makeQuery(id+"F9.opExtrude","SWEPT_FACE",FACE,{"disambiguationData":[OSD([subQ0])]})]});}
            var sketch = newSketch(context, id + "F17", { "sketchPlane" : qUnion([Q0])});
            skCircle(sketch, "E77", {"center": v(77.24, 0) * mm, "radius": 0.16 * mm});
            skSolve(sketch);
        }
        {
            var Q0;
            Q0=makeQuery(id+"F17.imprint","IMPRINT",FACE,{"disambiguationData":[TD([[makeQuery(id+"F17.imprint","IMPRINT",EDGE,{"derivedFrom":sQuery(id+"F17.wireOp",EDGE,"E77")}),1.0]])]});
            extrude(context, id + "F18", {"entities" : qUnion([Q0]), "operationType" : NewBodyOperationType.ADD, "depth" : 0.32 * mm, "offsetDistance" : 25.4 * mm});
        }
        {
            var Q0;
            Q0=makeQuery(id+"F9.opExtrude","CAP_EDGE",EDGE,{"disambiguationData":[OSD([sQuery(id+"F0.wireOp",EDGE,"E2.right")])],"isStart":false});
            var Q1;
            Q1=makeQuery(id+"F8.opExtrude","CAP_EDGE",EDGE,{"disambiguationData":[OSD([sQuery(id+"F0.wireOp",EDGE,"E2.right")])],"isStart":false});
            fillet(context, id + "F19", {"entities" : qUnion([Q0, Q1]), "radius" : 0.8 * mm, "tangentPropagation" : true, "allowEdgeOverflow" : false});
        }
        {
            var Q0;
            Q0=makeQuery(id+"F2.opExtrude","SWEPT_FACE",FACE,{"disambiguationData":[OSD([sQuery(id+"F0.wireOp",EDGE,"E6.top")])]});
            var sketch = newSketch(context, id + "F20", { "sketchPlane" : qUnion([Q0])});
            skCircle(sketch, "E78", {"center": v(-70, -3.96) * mm, "radius": 2.38 * mm});
            skCircle(sketch, "E79", {"center": v(-70, -11.91) * mm, "radius": 2.38 * mm});
            skCircle(sketch, "E80", {"center": v(-77.96, -11.91) * mm, "radius": 2.38 * mm});
            skCircle(sketch, "E81", {"center": v(-77.96, -3.96) * mm, "radius": 2.38 * mm});
            skLineSegment(sketch, "E82", {"start": v(-70.02, -15.88) * mm, "end": v(-70.02, 0) * mm, "construction": true});
            skLineSegment(sketch, "E83", {"start": v(-77.97, 0) * mm, "end": v(-77.97, -15.88) * mm, "construction": true});
            skLineSegment(sketch, "E84", {"start": v(-97.78, -3.96) * mm, "end": v(-66.03, -3.96) * mm, "construction": true});
            skLineSegment(sketch, "E85", {"start": v(-97.78, -11.91) * mm, "end": v(-66.03, -11.91) * mm, "construction": true});
            skLineSegment(sketch, "E86", {"start": v(-81.9, -15.88) * mm, "end": v(-81.9, 0) * mm, "construction": true});
            skCircle(sketch, "E87.MirrorC", {"center": v(-85.86, -11.91) * mm, "radius": 2.38 * mm});
            skCircle(sketch, "E88.MirrorC", {"center": v(-93.8, -11.91) * mm, "radius": 2.38 * mm});
            skCircle(sketch, "E89.MirrorC", {"center": v(-93.8, -3.96) * mm, "radius": 2.38 * mm});
            skCircle(sketch, "E90.MirrorC", {"center": v(-85.86, -3.96) * mm, "radius": 2.38 * mm});
            skSolve(sketch);
        }
        {
            var Q0;
            Q0=makeQuery(id+"F20.imprint","IMPRINT",FACE,{"disambiguationData":[TD([[makeQuery(id+"F20.imprint","IMPRINT",EDGE,{"derivedFrom":sQuery(id+"F20.wireOp",EDGE,"E81")}),1.0]])]});
            var Q1;
            Q1=makeQuery(id+"F20.imprint","IMPRINT",FACE,{"disambiguationData":[TD([[makeQuery(id+"F20.imprint","IMPRINT",EDGE,{"derivedFrom":sQuery(id+"F20.wireOp",EDGE,"E87.MirrorC")}),-1.0]])]});
            var Q2;
            Q2=makeQuery(id+"F20.imprint","IMPRINT",FACE,{"disambiguationData":[TD([[makeQuery(id+"F20.imprint","IMPRINT",EDGE,{"derivedFrom":sQuery(id+"F20.wireOp",EDGE,"E88.MirrorC")}),-1.0]])]});
            var Q3;
            Q3=makeQuery(id+"F20.imprint","IMPRINT",FACE,{"disambiguationData":[TD([[makeQuery(id+"F20.imprint","IMPRINT",EDGE,{"derivedFrom":sQuery(id+"F20.wireOp",EDGE,"E90.MirrorC")}),-1.0]])]});
            var Q4;
            Q4=makeQuery(id+"F20.imprint","IMPRINT",FACE,{"disambiguationData":[TD([[makeQuery(id+"F20.imprint","IMPRINT",EDGE,{"derivedFrom":sQuery(id+"F20.wireOp",EDGE,"E89.MirrorC")}),-1.0]])]});
            var Q5;
            Q5=makeQuery(id+"F20.imprint","IMPRINT",FACE,{"disambiguationData":[TD([[makeQuery(id+"F20.imprint","IMPRINT",EDGE,{"derivedFrom":sQuery(id+"F20.wireOp",EDGE,"E80")}),1.0]])]});
            var Q6;
            Q6=makeQuery(id+"F20.imprint","IMPRINT",FACE,{"disambiguationData":[TD([[makeQuery(id+"F20.imprint","IMPRINT",EDGE,{"derivedFrom":sQuery(id+"F20.wireOp",EDGE,"E79")}),1.0]])]});
            var Q7;
            Q7=makeQuery(id+"F20.imprint","IMPRINT",FACE,{"disambiguationData":[TD([[makeQuery(id+"F20.imprint","IMPRINT",EDGE,{"derivedFrom":sQuery(id+"F20.wireOp",EDGE,"E78")}),1.0]])]});
            extrude(context, id + "F21", {"entities" : qUnion([Q0, Q1, Q2, Q3, Q4, Q5, Q6, Q7]), "operationType" : NewBodyOperationType.ADD, "depth" : 1.59 * mm, "offsetDistance" : 25.4 * mm});
        }
        {
            var Q0;
            Q0=makeQuery(id+"F2.opExtrude","SWEPT_FACE",FACE,{"disambiguationData":[OSD([sQuery(id+"F0.wireOp",EDGE,"E5.bottom")])]});
            var sketch = newSketch(context, id + "F22", { "sketchPlane" : qUnion([Q0])});
            skLineSegment(sketch, "E91.top", {"start": v(-67.62, -14.29) * mm, "end": v(-69.2, -14.29) * mm});
            skLineSegment(sketch, "E91.left", {"start": v(-67.62, -15.88) * mm, "end": v(-67.62, -14.29) * mm});
            skLineSegment(sketch, "E91.right", {"start": v(-69.2, -15.08) * mm, "end": v(-69.2, -14.29) * mm});
            skLineSegment(sketch, "E92.bottom", {"start": v(-69.2, -14.29) * mm, "end": v(-67.62, -14.29) * mm});
            skLineSegment(sketch, "E92.top", {"start": v(-69.2, -15.08) * mm, "end": v(-67.62, -15.08) * mm});
            skLineSegment(sketch, "E92.left", {"start": v(-69.2, -14.29) * mm, "end": v(-69.2, -15.08) * mm});
            skLineSegment(sketch, "E92.right", {"start": v(-67.62, -14.29) * mm, "end": v(-67.62, -15.08) * mm});
            skPoint(sketch, "E93", {"position": v(-68.42, -15.46) * mm});
            skLineSegment(sketch, "E94", {"start": v(-81.9, -15.88) * mm, "end": v(-81.9, 0) * mm, "construction": true});
            skLineSegment(sketch, "E95.MirrorCS", {"start": v(-94.6, -15.08) * mm, "end": v(-94.6, -14.29) * mm});
            skLineSegment(sketch, "E96.MirrorCS", {"start": v(-94.6, -15.08) * mm, "end": v(-96.2, -15.08) * mm});
            skLineSegment(sketch, "E97.MirrorCS", {"start": v(-94.6, -14.29) * mm, "end": v(-96.2, -14.29) * mm});
            skLineSegment(sketch, "E98.MirrorCS", {"start": v(-96.2, -14.29) * mm, "end": v(-96.2, -15.08) * mm});
            skPoint(sketch, "E99.MirrorP", {"position": v(-95.4, -15.46) * mm});
            skSolve(sketch);
        }
        {
            var Q0;
            Q0=makeQuery(id+"F22.imprint","IMPRINT",FACE,{"disambiguationData":[TD([[makeQuery(id+"F22.imprint","IMPRINT",EDGE,{"derivedFrom":sQuery(id+"F22.wireOp",EDGE,"E92.bottom")}),-1.0]])]});
            var Q1;
            Q1=makeQuery(id+"F22.imprint","IMPRINT",FACE,{"disambiguationData":[TD([[makeQuery(id+"F22.imprint","IMPRINT",EDGE,{"derivedFrom":sQuery(id+"F22.wireOp",EDGE,"E95.MirrorCS")}),1.0]])]});
            extrude(context, id + "F23", {"entities" : qUnion([Q0, Q1]), "operationType" : NewBodyOperationType.ADD, "depth" : 25.4 * mm, "offsetDistance" : 25.4 * mm});
        }
        {
            var Q0;
            Q0=sQuery(id+"F22.wireOp",VERTEX,"E93");
            var Q1;
            Q1=sQuery(id+"F22.wireOp",VERTEX,"E99.MirrorP");
            var Q2;
            Q2=makeQuery(id+"F2.opExtrude","SWEPT_BODY",BODY,{"disambiguationData":[OSD([sQuery(id+"F0.wireOp",EDGE,"E5.bottom"),sQuery(id+"F0.wireOp",EDGE,"E5.top"),sQuery(id+"F0.wireOp",EDGE,"E5.left"),sQuery(id+"F0.wireOp",EDGE,"E5.right"),sQuery(id+"F0.wireOp",EDGE,"E6.bottom"),sQuery(id+"F0.wireOp",EDGE,"E6.top"),sQuery(id+"F0.wireOp",EDGE,"E6.left"),sQuery(id+"F0.wireOp",EDGE,"E6.right")])]});
            hole(context, id + "F24", {"style" : HoleStyle.SIMPLE, "endStyle" : HoleEndStyle.BLIND, "holeDiameter" : 0.32 * mm, "majorDiameter" : 6.35 * mm, "holeDepth" : 0.32 * mm, "isTappedThrough" : true, "tappedDepth" : 12.7 * mm, "tapClearance" : 3, "locations" : qUnion([Q0, Q1]), "scope" : qUnion([Q2])});
        }
        {
            var Q0;
            {var subQ3=sQuery(id+"F0.wireOp",EDGE,"E7.bottom");Q0=makeQuery(id+"F0.imprint","IMPRINT",FACE,{"disambiguationData":[TD([[makeQuery(id+"F0.imprint","IMPRINT",EDGE,{"derivedFrom":subQ3}),-1.0]])]});}
            var Q1;
            Q1=makeQuery(id+"F0.imprint","IMPRINT",FACE,{"disambiguationData":[TD([[makeQuery(id+"F0.imprint","IMPRINT",EDGE,{"derivedFrom":sQuery(id+"F0.wireOp",EDGE,"E8.right")}),1.0]])]});
            extrude(context, id + "F25", {"entities" : qUnion([Q0, Q1]), "depth" : 0.8 * mm, "offsetDistance" : 25.4 * mm});
        }
        {
            var Q0;
            {var subQ3=sQuery(id+"F0.wireOp",EDGE,"E7.bottom");Q0=makeQuery(id+"F0.imprint","IMPRINT",FACE,{"disambiguationData":[TD([[makeQuery(id+"F0.imprint","IMPRINT",EDGE,{"derivedFrom":subQ3}),-1.0]])]});}
            extrude(context, id + "F26", {"entities" : qUnion([Q0]), "operationType" : NewBodyOperationType.ADD, "oppositeDirection" : true, "depth" : 0.8 * mm, "offsetDistance" : 25.4 * mm});
        }
        {
            var Q0;
            Q0=makeQuery(id+"F0.imprint","IMPRINT",FACE,{"disambiguationData":[TD([[makeQuery(id+"F0.imprint","IMPRINT",EDGE,{"derivedFrom":sQuery(id+"F0.wireOp",EDGE,"E8.right")}),1.0]])]});
            extrude(context, id + "F27", {"entities" : qUnion([Q0]), "operationType" : NewBodyOperationType.ADD, "oppositeDirection" : true, "depth" : 0.8 * mm, "offsetDistance" : 25.4 * mm});
        }
        {
            var Q0;
            {var subQ0=sQuery(id+"F0.wireOp",EDGE,"E7.bottom");Q0=makeQuery(id+"F26.boolean.opBoolean","MERGE",FACE,{"derivedFrom":[makeQuery(id+"F25.opExtrude","SWEPT_FACE",FACE,{"disambiguationData":[OSD([subQ0])]}),makeQuery(id+"F26.opExtrude","SWEPT_FACE",FACE,{"disambiguationData":[OSD([subQ0])]})]});}
            var sketch = newSketch(context, id + "F28", { "sketchPlane" : qUnion([Q0])});
            skPoint(sketch, "E100", {"position": v(-9.55, 0) * mm});
            skPoint(sketch, "E101", {"position": v(-39.72, 0) * mm});
            skCircle(sketch, "E102", {"center": v(-9.55, 0) * mm, "radius": 0.16 * mm});
            skCircle(sketch, "E103", {"center": v(-39.72, 0) * mm, "radius": 0.16 * mm});
            skSolve(sketch);
        }
        {
            var Q0;
            Q0=makeQuery(id+"F28.imprint","IMPRINT",FACE,{"disambiguationData":[TD([[makeQuery(id+"F28.imprint","IMPRINT",EDGE,{"derivedFrom":sQuery(id+"F28.wireOp",EDGE,"E102")}),1.0]])]});
            extrude(context, id + "F29", {"entities" : qUnion([Q0]), "operationType" : NewBodyOperationType.ADD, "depth" : 0.32 * mm, "offsetDistance" : 25.4 * mm});
        }
        {
            var Q0;
            Q0=makeQuery(id+"F28.imprint","IMPRINT",FACE,{"disambiguationData":[TD([[makeQuery(id+"F28.imprint","IMPRINT",EDGE,{"derivedFrom":sQuery(id+"F28.wireOp",EDGE,"E103")}),1.0]])]});
            extrude(context, id + "F30", {"entities" : qUnion([Q0]), "operationType" : NewBodyOperationType.ADD, "depth" : 0.32 * mm, "offsetDistance" : 25.4 * mm});
        }
        {
            var Q0;
            Q0=makeQuery(id+"F0.imprint","IMPRINT",FACE,{"disambiguationData":[TD([[makeQuery(id+"F0.imprint","IMPRINT",EDGE,{"derivedFrom":sQuery(id+"F0.wireOp",EDGE,"E29.bottom")}),-1.0]])]});
            extrude(context, id + "F31", {"entities" : qUnion([Q0]), "depth" : 15.88 * mm, "offsetDistance" : 25.4 * mm});
        }
        {
            var Q0;
            Q0=makeQuery(id+"F31.opExtrude","SWEPT_FACE",FACE,{"disambiguationData":[OSD([sQuery(id+"F0.wireOp",EDGE,"E29.top")])]});
            var sketch = newSketch(context, id + "F32", { "sketchPlane" : qUnion([Q0])});
            skLineSegment(sketch, "E104", {"start": v(52.73, -15.88) * mm, "end": v(52.73, 0) * mm, "construction": true});
            skCircle(sketch, "E105", {"center": v(52.73, -11.91) * mm, "radius": 2.38 * mm});
            skCircle(sketch, "E106", {"center": v(52.73, -3.96) * mm, "radius": 2.38 * mm});
            skSolve(sketch);
        }
        {
            var Q0;
            Q0=makeQuery(id+"F32.imprint","IMPRINT",FACE,{"disambiguationData":[TD([[makeQuery(id+"F32.imprint","IMPRINT",EDGE,{"derivedFrom":sQuery(id+"F32.wireOp",EDGE,"E105")}),1.0]])]});
            var Q1;
            Q1=makeQuery(id+"F32.imprint","IMPRINT",FACE,{"disambiguationData":[TD([[makeQuery(id+"F32.imprint","IMPRINT",EDGE,{"derivedFrom":sQuery(id+"F32.wireOp",EDGE,"E106")}),1.0]])]});
            extrude(context, id + "F33", {"entities" : qUnion([Q0, Q1]), "operationType" : NewBodyOperationType.ADD, "depth" : 1.59 * mm, "offsetDistance" : 25.4 * mm});
        }
        {
            var Q0;
            Q0=makeQuery(id+"F0.imprint","IMPRINT",FACE,{"disambiguationData":[TD([[makeQuery(id+"F0.imprint","IMPRINT",EDGE,{"derivedFrom":sQuery(id+"F0.wireOp",EDGE,"E32.bottom")}),-1.0]])]});
            extrude(context, id + "F34", {"entities" : qUnion([Q0]), "depth" : 0.32 * mm, "offsetDistance" : 25.4 * mm});
        }
        {
            var Q0;
            Q0=makeQuery(id+"F0.imprint","IMPRINT",FACE,{"disambiguationData":[TD([[makeQuery(id+"F0.imprint","IMPRINT",EDGE,{"derivedFrom":sQuery(id+"F0.wireOp",EDGE,"E32.bottom")}),-1.0]])]});
            extrude(context, id + "F35", {"entities" : qUnion([Q0]), "operationType" : NewBodyOperationType.ADD, "oppositeDirection" : true, "depth" : 0.32 * mm, "offsetDistance" : 25.4 * mm});
        }
        {
            var Q0;
            Q0=makeQuery(id+"F34.opExtrude","CAP_EDGE",EDGE,{"disambiguationData":[OSD([sQuery(id+"F0.wireOp",EDGE,"E32.right")])],"isStart":false});
            var Q1;
            Q1=makeQuery(id+"F35.opExtrude","CAP_EDGE",EDGE,{"disambiguationData":[OSD([sQuery(id+"F0.wireOp",EDGE,"E32.right")])],"isStart":false});
            fillet(context, id + "F36", {"entities" : qUnion([Q0, Q1]), "radius" : 0.32 * mm, "tangentPropagation" : true, "allowEdgeOverflow" : false});
        }
        {
            var Q0;
            {var subQ0=sQuery(id+"F0.wireOp",EDGE,"E32.bottom");Q0=makeQuery(id+"F35.boolean.opBoolean","MERGE",FACE,{"derivedFrom":[makeQuery(id+"F34.opExtrude","SWEPT_FACE",FACE,{"disambiguationData":[OSD([subQ0])]}),makeQuery(id+"F35.opExtrude","SWEPT_FACE",FACE,{"disambiguationData":[OSD([subQ0])]})]});}
            var sketch = newSketch(context, id + "F37", { "sketchPlane" : qUnion([Q0])});
            skCircle(sketch, "E107", {"center": v(-97.86, 0) * mm, "radius": 0.16 * mm});
            skSolve(sketch);
        }
        {
            var Q0;
            Q0=makeQuery(id+"F37.imprint","IMPRINT",FACE,{"disambiguationData":[TD([[makeQuery(id+"F37.imprint","IMPRINT",EDGE,{"derivedFrom":sQuery(id+"F37.wireOp",EDGE,"E107")}),1.0]])]});
            extrude(context, id + "F38", {"entities" : qUnion([Q0]), "operationType" : NewBodyOperationType.ADD, "depth" : 0.32 * mm, "offsetDistance" : 25.4 * mm});
        }
    });
